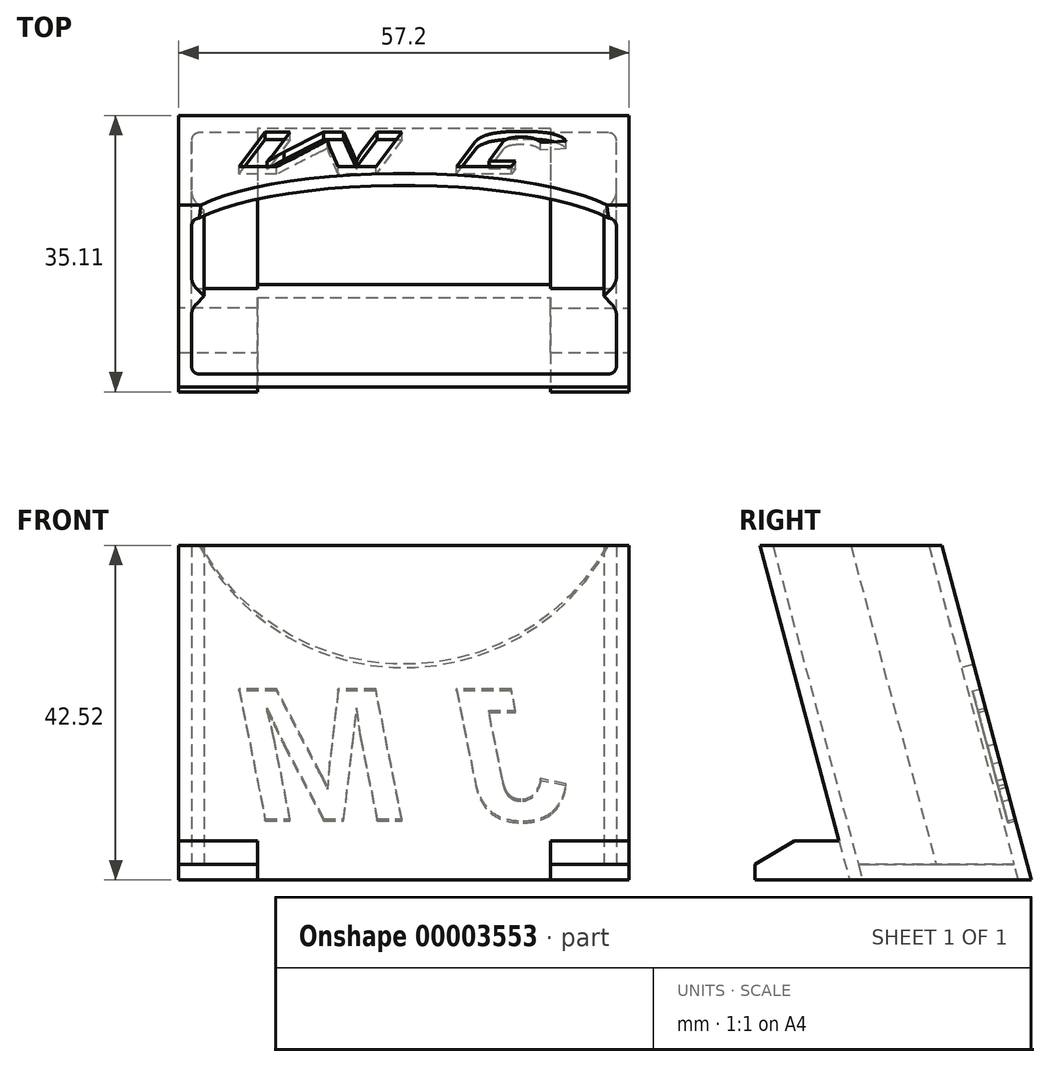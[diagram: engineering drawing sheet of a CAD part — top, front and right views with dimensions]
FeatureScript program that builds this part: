
annotation { "Feature Type Name" : "Feature", "Feature Type Description" : "" }
export const myFeature = defineFeature(function(context is Context, id is Id, definition is map)
    precondition{}
    {
        {
            var Q0;
            Q0=qCreatedBy(makeId("Top.planeOp"),FACE);
            var sketch = newSketch(context, id + "F0", { "sketchPlane" : qUnion([Q0])});
            skLineSegment(sketch, "E0", {"start": v(0, 0) * mm, "end": v(-26, 0) * mm});
            skLineSegment(sketch, "E1", {"start": v(-27, -1) * mm, "end": v(-27, -7.13) * mm});
            skLineSegment(sketch, "E2", {"start": v(-26.41, -8.54) * mm, "end": v(-25.4, -9.56) * mm});
            skLineSegment(sketch, "E3", {"start": v(-25.4, -9.56) * mm, "end": v(-28.6, -9.56) * mm});
            skLineSegment(sketch, "E4", {"start": v(-28.6, -9.56) * mm, "end": v(-28.6, 1.6) * mm});
            skLineSegment(sketch, "E5", {"start": v(-28.6, 1.6) * mm, "end": v(0, 1.6) * mm});
            skLineSegment(sketch, "E6", {"start": v(0, 1.6) * mm, "end": v(0, 0) * mm});
            skLineSegment(sketch, "E7", {"start": v(-28.6, -4.48) * mm, "end": v(-27, -4.48) * mm, "construction": true});
            skPoint(sketch, "E8.visualSharp", {"position": v(-27, 0) * mm});
            skArc(sketch, "E8.filletArc", {"start": v(-26, 0) * mm, "mid": v(-26.7, -0.3) * mm, "end": v(-27, -1) * mm});
            skPoint(sketch, "E9.visualSharp", {"position": v(-27, -7.96) * mm});
            skArc(sketch, "E9.filletArc", {"start": v(-27, -7.13) * mm, "mid": v(-26.85, -7.9) * mm, "end": v(-26.41, -8.54) * mm});
            skSolve(sketch);
        }
        {
            var Q0;
            Q0=makeQuery(id+"F0.imprint","IMPRINT",FACE,{"disambiguationData":[TD([[makeQuery(id+"F0.imprint","IMPRINT",EDGE,{"derivedFrom":sQuery(id+"F0.wireOp",EDGE,"E0")}),-1.0]])]});
            extrude(context, id + "F1", {"entities" : qUnion([Q0]), "depth" : 5 * mm});
        }
        {
            var Q0;
            Q0=makeQuery(id+"F1.opExtrude","SWEPT_BODY",BODY,{"disambiguationData":[OSD([sQuery(id+"F0.wireOp",EDGE,"E0"),sQuery(id+"F0.wireOp",EDGE,"E1"),sQuery(id+"F0.wireOp",EDGE,"E2"),sQuery(id+"F0.wireOp",EDGE,"E3"),sQuery(id+"F0.wireOp",EDGE,"E4"),sQuery(id+"F0.wireOp",EDGE,"E5"),sQuery(id+"F0.wireOp",EDGE,"E6"),sQuery(id+"F0.wireOp",EDGE,"E8.filletArc"),sQuery(id+"F0.wireOp",EDGE,"E9.filletArc")])]});
            var Q1;
            Q1=makeQuery(id+"F1.opExtrude","SWEPT_FACE",FACE,{"disambiguationData":[OSD([sQuery(id+"F0.wireOp",EDGE,"E3")])]});
            mirror(context, id + "F2", {"entities" : qUnion([Q0]), "mirrorPlane" : qUnion([Q1])});
        }
        {
            var Q0;
            Q0=makeQuery(id+"F1.opExtrude","SWEPT_BODY",BODY,{"disambiguationData":[OSD([sQuery(id+"F0.wireOp",EDGE,"E0"),sQuery(id+"F0.wireOp",EDGE,"E1"),sQuery(id+"F0.wireOp",EDGE,"E2"),sQuery(id+"F0.wireOp",EDGE,"E3"),sQuery(id+"F0.wireOp",EDGE,"E4"),sQuery(id+"F0.wireOp",EDGE,"E5"),sQuery(id+"F0.wireOp",EDGE,"E6"),sQuery(id+"F0.wireOp",EDGE,"E8.filletArc"),sQuery(id+"F0.wireOp",EDGE,"E9.filletArc")])]});
            var Q1;
            Q1=makeQuery(id+"F2.opPattern","COPY",BODY,{"derivedFrom":makeQuery(id+"F1.opExtrude","SWEPT_BODY",BODY,{"disambiguationData":[OSD([sQuery(id+"F0.wireOp",EDGE,"E0"),sQuery(id+"F0.wireOp",EDGE,"E1"),sQuery(id+"F0.wireOp",EDGE,"E2"),sQuery(id+"F0.wireOp",EDGE,"E3"),sQuery(id+"F0.wireOp",EDGE,"E4"),sQuery(id+"F0.wireOp",EDGE,"E5"),sQuery(id+"F0.wireOp",EDGE,"E6"),sQuery(id+"F0.wireOp",EDGE,"E8.filletArc"),sQuery(id+"F0.wireOp",EDGE,"E9.filletArc")])]}),"instanceName":"1"});
            var Q2;
            Q2=makeQuery(id+"F1.opExtrude","SWEPT_FACE",FACE,{"disambiguationData":[OSD([sQuery(id+"F0.wireOp",EDGE,"E6")])]});
            mirror(context, id + "F3", {"entities" : qUnion([Q0, Q1]), "mirrorPlane" : qUnion([Q2])});
        }
        {
            var Q0;
            Q0=makeQuery(id+"F1.opExtrude","SWEPT_BODY",BODY,{"disambiguationData":[OSD([sQuery(id+"F0.wireOp",EDGE,"E0"),sQuery(id+"F0.wireOp",EDGE,"E1"),sQuery(id+"F0.wireOp",EDGE,"E2"),sQuery(id+"F0.wireOp",EDGE,"E3"),sQuery(id+"F0.wireOp",EDGE,"E4"),sQuery(id+"F0.wireOp",EDGE,"E5"),sQuery(id+"F0.wireOp",EDGE,"E6"),sQuery(id+"F0.wireOp",EDGE,"E8.filletArc"),sQuery(id+"F0.wireOp",EDGE,"E9.filletArc")])]});
            var Q1;
            Q1=makeQuery(id+"F2.opPattern","COPY",BODY,{"derivedFrom":makeQuery(id+"F1.opExtrude","SWEPT_BODY",BODY,{"disambiguationData":[OSD([sQuery(id+"F0.wireOp",EDGE,"E0"),sQuery(id+"F0.wireOp",EDGE,"E1"),sQuery(id+"F0.wireOp",EDGE,"E2"),sQuery(id+"F0.wireOp",EDGE,"E3"),sQuery(id+"F0.wireOp",EDGE,"E4"),sQuery(id+"F0.wireOp",EDGE,"E5"),sQuery(id+"F0.wireOp",EDGE,"E6"),sQuery(id+"F0.wireOp",EDGE,"E8.filletArc"),sQuery(id+"F0.wireOp",EDGE,"E9.filletArc")])]}),"instanceName":"1"});
            var Q2;
            Q2=makeQuery(id+"F3.opPattern","COPY",BODY,{"derivedFrom":makeQuery(id+"F1.opExtrude","SWEPT_BODY",BODY,{"disambiguationData":[OSD([sQuery(id+"F0.wireOp",EDGE,"E0"),sQuery(id+"F0.wireOp",EDGE,"E1"),sQuery(id+"F0.wireOp",EDGE,"E2"),sQuery(id+"F0.wireOp",EDGE,"E3"),sQuery(id+"F0.wireOp",EDGE,"E4"),sQuery(id+"F0.wireOp",EDGE,"E5"),sQuery(id+"F0.wireOp",EDGE,"E6"),sQuery(id+"F0.wireOp",EDGE,"E8.filletArc"),sQuery(id+"F0.wireOp",EDGE,"E9.filletArc")])]}),"instanceName":"1"});
            var Q3;
            Q3=makeQuery(id+"F3.opPattern","COPY",BODY,{"derivedFrom":makeQuery(id+"F2.opPattern","COPY",BODY,{"derivedFrom":makeQuery(id+"F1.opExtrude","SWEPT_BODY",BODY,{"disambiguationData":[OSD([sQuery(id+"F0.wireOp",EDGE,"E0"),sQuery(id+"F0.wireOp",EDGE,"E1"),sQuery(id+"F0.wireOp",EDGE,"E2"),sQuery(id+"F0.wireOp",EDGE,"E3"),sQuery(id+"F0.wireOp",EDGE,"E4"),sQuery(id+"F0.wireOp",EDGE,"E5"),sQuery(id+"F0.wireOp",EDGE,"E6"),sQuery(id+"F0.wireOp",EDGE,"E8.filletArc"),sQuery(id+"F0.wireOp",EDGE,"E9.filletArc")])]}),"instanceName":"1"}),"instanceName":"1"});
            booleanBodies(context, id + "F4", {"operationType" : BooleanOperationType.UNION, "tools" : qUnion([Q0, Q1, Q2, Q3])});
        }
        {
            var Q0;
            {var subQ0=makeQuery(id+"F1.opExtrude","CAP_FACE",FACE,{"disambiguationData":[OSD([sQuery(id+"F0.wireOp",EDGE,"E0"),sQuery(id+"F0.wireOp",EDGE,"E1"),sQuery(id+"F0.wireOp",EDGE,"E2"),sQuery(id+"F0.wireOp",EDGE,"E3"),sQuery(id+"F0.wireOp",EDGE,"E4"),sQuery(id+"F0.wireOp",EDGE,"E5"),sQuery(id+"F0.wireOp",EDGE,"E6"),sQuery(id+"F0.wireOp",EDGE,"E8.filletArc"),sQuery(id+"F0.wireOp",EDGE,"E9.filletArc")])],"isStart":false});var subQ1=makeQuery(id+"F2.opPattern","COPY",FACE,{"derivedFrom":subQ0,"instanceName":"1"});Q0=makeQuery(id+"F4.opBoolean","MERGE",FACE,{"derivedFrom":[subQ0,subQ1,makeQuery(id+"F3.opPattern","COPY",FACE,{"derivedFrom":subQ0,"instanceName":"1"}),makeQuery(id+"F3.opPattern","COPY",FACE,{"derivedFrom":subQ1,"instanceName":"1"})]});}
            extrude(context, id + "F5", {"entities" : qUnion([Q0]), "operationType" : NewBodyOperationType.ADD, "depth" : 45 * mm});
        }
        {
            var Q0;
            Q0=makeQuery(id+"F1.opExtrude","SWEPT_BODY",BODY,{"disambiguationData":[OSD([sQuery(id+"F0.wireOp",EDGE,"E0"),sQuery(id+"F0.wireOp",EDGE,"E1"),sQuery(id+"F0.wireOp",EDGE,"E2"),sQuery(id+"F0.wireOp",EDGE,"E3"),sQuery(id+"F0.wireOp",EDGE,"E4"),sQuery(id+"F0.wireOp",EDGE,"E5"),sQuery(id+"F0.wireOp",EDGE,"E6"),sQuery(id+"F0.wireOp",EDGE,"E8.filletArc"),sQuery(id+"F0.wireOp",EDGE,"E9.filletArc")])]});
            var Q1;
            {var subQ0=makeQuery(id+"F2.opPattern","COPY",EDGE,{"derivedFrom":makeQuery(id+"F1.opExtrude","CAP_EDGE",EDGE,{"disambiguationData":[OSD([sQuery(id+"F0.wireOp",EDGE,"E5")])],"isStart":true}),"instanceName":"1"});Q1=makeQuery(id+"F4.opBoolean","MERGE",EDGE,{"derivedFrom":[subQ0,makeQuery(id+"F3.opPattern","COPY",EDGE,{"derivedFrom":subQ0,"instanceName":"1"})]});}
            transform(context, id + "F6", {"entities" : qUnion([Q0]), "transformType" : TransformType.ROTATION, "transformAxis" : qUnion([Q1]), "angle" : 15 * degree, "makeCopy" : false});
        }
        {
            var Q0;
            {var subQ0=sQuery(id+"F0.wireOp",EDGE,"E4");var subQ1=makeQuery(id+"F1.opExtrude","SWEPT_FACE",FACE,{"disambiguationData":[OSD([subQ0])]});var subQ2=makeQuery(id+"F1.opExtrude","CAP_EDGE",EDGE,{"disambiguationData":[OSD([subQ0])],"isStart":false});Q0=makeQuery(id+"F5.boolean.opBoolean","MERGE",FACE,{"derivedFrom":[makeQuery(id+"F4.opBoolean","MERGE",FACE,{"derivedFrom":[makeQuery(id+"F3.opPattern","COPY",FACE,{"derivedFrom":subQ1,"instanceName":"1"}),makeQuery(id+"F3.opPattern","COPY",FACE,{"derivedFrom":makeQuery(id+"F2.opPattern","COPY",FACE,{"derivedFrom":subQ1,"instanceName":"1"}),"instanceName":"1"})]}),makeQuery(id+"F5.opExtrude","SWEPT_FACE",FACE,{"disambiguationData":[OSD([subQ0]),TDD([makeQuery(id+"F4.opBoolean","MERGE",EDGE,{"derivedFrom":[makeQuery(id+"F3.opPattern","COPY",EDGE,{"derivedFrom":subQ2,"instanceName":"1"}),makeQuery(id+"F3.opPattern","COPY",EDGE,{"derivedFrom":makeQuery(id+"F2.opPattern","COPY",EDGE,{"derivedFrom":subQ2,"instanceName":"1"}),"instanceName":"1"})]})])]})]});}
            var sketch = newSketch(context, id + "F7", { "sketchPlane" : qUnion([Q0])});
            skLineSegment(sketch, "E10", {"start": v(0.84, 5.78) * mm, "end": v(-22.27, 5.78) * mm});
            skLineSegment(sketch, "E11", {"start": v(-33.66, 48.3) * mm, "end": v(-10.55, 48.3) * mm});
            skSolve(sketch);
        }
        {
            var Q0;
            {var subQ3=sQuery(id+"F7.wireOp",EDGE,"E10");Q0=makeQuery(id+"F7.imprint","IMPRINT",FACE,{"disambiguationData":[TD([[makeQuery(id+"F7.imprint","IMPRINT",EDGE,{"derivedFrom":subQ3}),1.0]])]});}
            var Q1;
            {var subQ3=sQuery(id+"F7.wireOp",EDGE,"E11");Q1=makeQuery(id+"F7.imprint","IMPRINT",FACE,{"disambiguationData":[TD([[makeQuery(id+"F7.imprint","IMPRINT",EDGE,{"derivedFrom":subQ3}),1.0]])]});}
            extrude(context, id + "F8", {"entities" : qUnion([Q0, Q1]), "operationType" : NewBodyOperationType.REMOVE, "oppositeDirection" : true, "depth" : 60 * mm});
        }
        {
            var Q0;
            {var subQ0=sQuery(id+"F0.wireOp",EDGE,"E0");var subQ1=makeQuery(id+"F1.opExtrude","SWEPT_FACE",FACE,{"disambiguationData":[OSD([subQ0])]});var subQ2=makeQuery(id+"F1.opExtrude","CAP_EDGE",EDGE,{"disambiguationData":[OSD([subQ0])],"isStart":false});Q0=makeQuery(id+"F5.boolean.opBoolean","MERGE",FACE,{"derivedFrom":[makeQuery(id+"F4.opBoolean","MERGE",FACE,{"derivedFrom":[subQ1,makeQuery(id+"F3.opPattern","COPY",FACE,{"derivedFrom":subQ1,"instanceName":"1"})]}),makeQuery(id+"F5.opExtrude","SWEPT_FACE",FACE,{"disambiguationData":[OSD([subQ0]),TDD([makeQuery(id+"F4.opBoolean","MERGE",EDGE,{"derivedFrom":[subQ2,makeQuery(id+"F3.opPattern","COPY",EDGE,{"derivedFrom":subQ2,"instanceName":"1"})]})])]})]});}
            var sketch = newSketch(context, id + "F9", { "sketchPlane" : qUnion([Q0])});
            skArc(sketch, "E12", {"start": v(-26, 49.81) * mm, "mid": v(0, 33.74) * mm, "end": v(26, 49.81) * mm});
            skSolve(sketch);
        }
        {
            var Q0;
            Q0=makeQuery(id+"F9.imprint","IMPRINT",FACE,{"disambiguationData":[TD([[makeQuery(id+"F9.imprint","IMPRINT",EDGE,{"derivedFrom":sQuery(id+"F9.wireOp",EDGE,"395de606-422e-434a-8833-f607af7b23ea")}),1.0]])]});
            var Q1;
            Q1=makeQuery(id+"F9.imprint","IMPRINT",FACE,{"disambiguationData":[TD([[makeQuery(id+"F9.imprint","IMPRINT",EDGE,{"derivedFrom":sQuery(id+"F9.wireOp",EDGE,"E12")}),1.0]])]});
            extrude(context, id + "F10", {"entities" : qUnion([Q0, Q1]), "operationType" : NewBodyOperationType.REMOVE, "oppositeDirection" : true, "depth" : 25 * mm});
        }
        {
            var Q0;
            {var subQ0=sQuery(id+"F0.wireOp",EDGE,"E4");var subQ1=makeQuery(id+"F1.opExtrude","SWEPT_FACE",FACE,{"disambiguationData":[OSD([subQ0])]});var subQ2=makeQuery(id+"F1.opExtrude","CAP_EDGE",EDGE,{"disambiguationData":[OSD([subQ0])],"isStart":false});Q0=makeQuery(id+"F5.boolean.opBoolean","MERGE",FACE,{"derivedFrom":[makeQuery(id+"F4.opBoolean","MERGE",FACE,{"derivedFrom":[makeQuery(id+"F3.opPattern","COPY",FACE,{"derivedFrom":subQ1,"instanceName":"1"}),makeQuery(id+"F3.opPattern","COPY",FACE,{"derivedFrom":makeQuery(id+"F2.opPattern","COPY",FACE,{"derivedFrom":subQ1,"instanceName":"1"}),"instanceName":"1"})]}),makeQuery(id+"F5.opExtrude","SWEPT_FACE",FACE,{"disambiguationData":[OSD([subQ0]),TDD([makeQuery(id+"F4.opBoolean","MERGE",EDGE,{"derivedFrom":[makeQuery(id+"F3.opPattern","COPY",EDGE,{"derivedFrom":subQ2,"instanceName":"1"}),makeQuery(id+"F3.opPattern","COPY",EDGE,{"derivedFrom":makeQuery(id+"F2.opPattern","COPY",EDGE,{"derivedFrom":subQ2,"instanceName":"1"}),"instanceName":"1"})]})])]})]});}
            var sketch = newSketch(context, id + "F11", { "sketchPlane" : qUnion([Q0])});
            skLineSegment(sketch, "E13.bottom", {"start": v(-22.27, 5.78) * mm, "end": v(-34.27, 5.78) * mm});
            skLineSegment(sketch, "E13.right", {"start": v(-34.27, 5.78) * mm, "end": v(-34.27, 10.78) * mm});
            skLineSegment(sketch, "E14", {"start": v(-34.27, 10.78) * mm, "end": v(-23.6, 10.78) * mm});
            skSolve(sketch);
        }
        {
            var Q0;
            {var subQ5=sQuery(id+"F11.wireOp",EDGE,"E13.bottom");Q0=makeQuery(id+"F11.imprint","IMPRINT",FACE,{"disambiguationData":[TD([[makeQuery(id+"F11.imprint","IMPRINT",EDGE,{"derivedFrom":subQ5}),-1.0]])]});}
            extrude(context, id + "F12", {"entities" : qUnion([Q0]), "oppositeDirection" : true, "depth" : 6 * mm});
        }
        {
            var Q0;
            {var subQ4=sQuery(id+"F11.wireOp",EDGE,"E13.bottom");Q0=makeQuery(id+"F11.imprint","IMPRINT",FACE,{"disambiguationData":[TD([[makeQuery(id+"F11.imprint","IMPRINT",EDGE,{"derivedFrom":subQ4}),-1.0]])]});}
            extrude(context, id + "F13", {"entities" : qUnion([Q0]), "operationType" : NewBodyOperationType.ADD, "oppositeDirection" : true, "depth" : 10 * mm});
        }
        {
            var Q0;
            {var subQ0=sQuery(id+"F11.wireOp",EDGE,"E13.right");var subQ1=sQuery(id+"F11.wireOp",EDGE,"E14");Q0=makeQuery(id+"F13.boolean.opBoolean","MERGE",EDGE,{"derivedFrom":[makeQuery(id+"F12.opExtrude","SWEPT_EDGE",EDGE,{"disambiguationData":[OSD([subQ0,subQ1])]}),makeQuery(id+"F13.opExtrude","SWEPT_EDGE",EDGE,{"disambiguationData":[OSD([subQ0,subQ1])]})]});}
            chamfer(context, id + "F14", {"entities" : qUnion([Q0]), "chamferType" : ChamferType.TWO_OFFSETS, "width1" : 5 * mm, "oppositeDirection" : false, "width2" : 3 * mm});
        }
        {
            var Q0;
            {var subQ0=sQuery(id+"F0.wireOp",EDGE,"E4");var subQ1=makeQuery(id+"F1.opExtrude","SWEPT_FACE",FACE,{"disambiguationData":[OSD([subQ0])]});var subQ2=makeQuery(id+"F1.opExtrude","CAP_EDGE",EDGE,{"disambiguationData":[OSD([subQ0])],"isStart":false});Q0=makeQuery(id+"F5.boolean.opBoolean","MERGE",FACE,{"derivedFrom":[makeQuery(id+"F4.opBoolean","MERGE",FACE,{"derivedFrom":[subQ1,makeQuery(id+"F2.opPattern","COPY",FACE,{"derivedFrom":subQ1,"instanceName":"1"})]}),makeQuery(id+"F5.opExtrude","SWEPT_FACE",FACE,{"disambiguationData":[OSD([subQ0]),TDD([makeQuery(id+"F4.opBoolean","MERGE",EDGE,{"derivedFrom":[subQ2,makeQuery(id+"F2.opPattern","COPY",EDGE,{"derivedFrom":subQ2,"instanceName":"1"})]})])]})]});}
            var sketch = newSketch(context, id + "F15", { "sketchPlane" : qUnion([Q0])});
            skLineSegment(sketch, "E15", {"start": v(22.27, 5.78) * mm, "end": v(34.27, 5.78) * mm});
            skLineSegment(sketch, "E16", {"start": v(34.27, 5.78) * mm, "end": v(34.27, 10.78) * mm});
            skLineSegment(sketch, "E17", {"start": v(34.27, 10.78) * mm, "end": v(23.6, 10.78) * mm});
            skSolve(sketch);
        }
        {
            var Q0;
            {var subQ6=sQuery(id+"F15.wireOp",EDGE,"E15");Q0=makeQuery(id+"F15.imprint","IMPRINT",FACE,{"disambiguationData":[TD([[makeQuery(id+"F15.imprint","IMPRINT",EDGE,{"derivedFrom":subQ6}),1.0]])]});}
            extrude(context, id + "F16", {"entities" : qUnion([Q0]), "operationType" : NewBodyOperationType.ADD, "oppositeDirection" : true, "depth" : 10 * mm});
        }
        {
            var Q0;
            Q0=makeQuery(id+"F16.opExtrude","SWEPT_EDGE",EDGE,{"disambiguationData":[OSD([sQuery(id+"F15.wireOp",EDGE,"E16"),sQuery(id+"F15.wireOp",EDGE,"E17")])]});
            chamfer(context, id + "F17", {"entities" : qUnion([Q0]), "chamferType" : ChamferType.TWO_OFFSETS, "width1" : 5 * mm, "oppositeDirection" : true, "width2" : 3 * mm, "tangentPropagation" : true});
        }
        {
            var Q0;
            {var subQ0=sQuery(id+"F11.wireOp",EDGE,"E13.right");Q0=makeQuery(id+"F13.boolean.opBoolean","MERGE",FACE,{"derivedFrom":[makeQuery(id+"F12.opExtrude","SWEPT_FACE",FACE,{"disambiguationData":[OSD([subQ0])]}),makeQuery(id+"F13.opExtrude","SWEPT_FACE",FACE,{"disambiguationData":[OSD([subQ0])]})]});}
            var Q1;
            Q1=makeQuery(id+"F16.opExtrude","SWEPT_FACE",FACE,{"disambiguationData":[OSD([sQuery(id+"F15.wireOp",EDGE,"E16")])]});
            extrude(context, id + "F18", {"entities" : qUnion([Q0, Q1]), "operationType" : NewBodyOperationType.ADD, "oppositeDirection" : true, "depth" : 34 * mm});
        }
        {
            var Q0;
            {var subQ0=sQuery(id+"F0.wireOp",EDGE,"E5");var subQ1=makeQuery(id+"F1.opExtrude","SWEPT_FACE",FACE,{"disambiguationData":[OSD([subQ0])]});var subQ2=makeQuery(id+"F1.opExtrude","CAP_EDGE",EDGE,{"disambiguationData":[OSD([subQ0])],"isStart":false});Q0=makeQuery(id+"F5.boolean.opBoolean","MERGE",FACE,{"derivedFrom":[makeQuery(id+"F4.opBoolean","MERGE",FACE,{"derivedFrom":[subQ1,makeQuery(id+"F3.opPattern","COPY",FACE,{"derivedFrom":subQ1,"instanceName":"1"})]}),makeQuery(id+"F5.opExtrude","SWEPT_FACE",FACE,{"disambiguationData":[OSD([subQ0]),TDD([makeQuery(id+"F4.opBoolean","MERGE",EDGE,{"derivedFrom":[subQ2,makeQuery(id+"F3.opPattern","COPY",EDGE,{"derivedFrom":subQ2,"instanceName":"1"})]})])]})]});}
            var sketch = newSketch(context, id + "F19", { "sketchPlane" : qUnion([Q0])});
            skText(sketch, "E18", { "text": "J M", "fontName": "Arimo-BoldItalic.ttf"});
            const initialGuessF19  = {"E18": [-0.02092, 0.0134, 1, 0, 0.01789]};
            skSetInitialGuess(sketch, initialGuessF19);
            skSolve(sketch);
        }
        {
            var Q0;
            Q0=makeQuery(id+"F19.imprint","IMPRINT",FACE,{"disambiguationData":[TD([[makeQuery(id+"F19.imprint","IMPRINT",EDGE,{"derivedFrom":sQuery(id+"F19.wireOp",EDGE,"E18.sketch_text.stroke-0")}),-1.0]])]});
            var Q1;
            Q1=makeQuery(id+"F19.imprint","IMPRINT",FACE,{"disambiguationData":[TD([[makeQuery(id+"F19.imprint","IMPRINT",EDGE,{"derivedFrom":sQuery(id+"F19.wireOp",EDGE,"E18.sketch_text.stroke-17")}),-1.0]])]});
            var Q2;
            Q2=makeQuery(id+"F19.imprint","IMPRINT",FACE,{"disambiguationData":[TD([[makeQuery(id+"F19.imprint","IMPRINT",EDGE,{"derivedFrom":sQuery(id+"F19.wireOp",EDGE,"E18.sketch_text.stroke-24")}),-1.0]])]});
            var Q3;
            Q3=makeQuery(id+"F19.imprint","IMPRINT",FACE,{"disambiguationData":[TD([[makeQuery(id+"F19.imprint","IMPRINT",EDGE,{"derivedFrom":sQuery(id+"F19.wireOp",EDGE,"E18.sketch_text.stroke-45")}),-1.0]])]});
            var Q4;
            Q4=makeQuery(id+"F19.imprint","IMPRINT",FACE,{"disambiguationData":[TD([[makeQuery(id+"F19.imprint","IMPRINT",EDGE,{"derivedFrom":sQuery(id+"F19.wireOp",EDGE,"E18.sketch_text.stroke-60")}),-1.0]])]});
            var Q5;
            Q5=makeQuery(id+"F19.imprint","IMPRINT",FACE,{"disambiguationData":[TD([[makeQuery(id+"F19.imprint","IMPRINT",EDGE,{"derivedFrom":sQuery(id+"F19.wireOp",EDGE,"E18.sketch_text.stroke-56")}),-1.0]])]});
            var Q6;
            Q6=makeQuery(id+"F19.imprint","IMPRINT",FACE,{"disambiguationData":[TD([[makeQuery(id+"F19.imprint","IMPRINT",EDGE,{"derivedFrom":sQuery(id+"F19.wireOp",EDGE,"E18.sketch_text.stroke-52")}),-1.0]])]});
            var Q7;
            Q7=makeQuery(id+"F19.imprint","IMPRINT",FACE,{"disambiguationData":[TD([[makeQuery(id+"F19.imprint","IMPRINT",EDGE,{"derivedFrom":sQuery(id+"F19.wireOp",EDGE,"E18.sketch_text.stroke-64")}),-1.0]])]});
            extrude(context, id + "F20", {"entities" : qUnion([Q0, Q1, Q2, Q3, Q4, Q5, Q6, Q7]), "operationType" : NewBodyOperationType.REMOVE, "oppositeDirection" : true, "depth" : 1 * mm});
        }
        {
            var Q0;
            Q0=makeQuery(id+"F19.imprint","IMPRINT",FACE,{"disambiguationData":[TD([[makeQuery(id+"F19.imprint","IMPRINT",EDGE,{"derivedFrom":sQuery(id+"F19.wireOp",EDGE,"E18.sketch_text.stroke-14")}),-1.0]])]});
            var Q1;
            Q1=makeQuery(id+"F19.imprint","IMPRINT",FACE,{"disambiguationData":[TD([[makeQuery(id+"F19.imprint","IMPRINT",EDGE,{"derivedFrom":sQuery(id+"F19.wireOp",EDGE,"E18.sketch_text.stroke-0")}),-1.0]])]});
            extrude(context, id + "F21", {"entities" : qUnion([Q0, Q1]), "operationType" : NewBodyOperationType.REMOVE, "oppositeDirection" : true, "depth" : 1 * mm});
        }
    });
